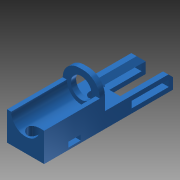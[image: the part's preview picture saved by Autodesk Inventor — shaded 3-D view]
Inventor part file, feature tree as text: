
AUTODESK INVENTOR PART (.ipt)
format: ipt  version: 2013 SP2 (Build 170200200, 200)  size: 194,560 bytes
history: native  units: in
note: dims shown in document units (in); Inventor stores cm internally (conversion verified against a paired STEP export)
features: extrude x10, sketch x8, fillet x1, chamfer x1
ambient origin geometry x8: Origin, YZ Plane, XZ Plane, XY Plane, X Axis, Y Axis, Z Axis, Center Point
bodies: Solid1 (feature_tree)
feature tree (20):
  sketch  "Sketch1"  dims[d5=1.063in d6=0.0in d11=0.5512in]
  extrude  "Extrusion1"  Depth=0.5512in
  extrude  "Extrusion6"  Depth=0.0787in
  extrude  "Extrusion5"  Depth=0.7087in
  extrude  "Extrusion7"  Depth=0.8661in
  fillet  "Fillet1"  Radius=0.0984in
  extrude  "Extrusion8"  Depth=0.315in
  extrude  "Extrusion9"  Depth=0.0984in
  extrude  "Extrusion10"  Depth=0.0787in TaperAngle=0.0deg
  extrude  "Extrusion11"  Depth=1.2992in TaperAngle=0.0deg
  extrude  "Extrusion12"  Depth=1.1811in TaperAngle=0.0deg
  extrude  "Extrusion13"  Depth=0.9055in
  chamfer  "Chamfer2"  [1 undecoded]
  sketch  "Sketch3"  dims[d12=0.3937in d13=0.0787in]
  sketch  "Sketch4"  dims[d18=0.5512in d19=0.7087in]
  sketch  "Sketch5"  dims[d20=1.1811in d21=0.0in d22=0.8661in d25=0.0984in d26=0.0in]
  sketch  "Sketch6"  dims[d27=0.0787in d28=0.0in d29=0.315in]
  sketch  "Sketch7"  dims[d32=0.2362in d33=0.0984in]
  sketch  "Sketch8"  dims[d34=0.0394in d35=0.0787in d36=0.0in]
  sketch  "Sketch9"  dims[d37=0.2953in d38=1.2992in d39=0.0in d41=1.1811in d42=0.0in d45=0.9055in d47=0.0in d49=0.126in d51=0.3937in d52=0.0in d55=0.7087in d56=0.2362in d57=0.2362in d58=0.1575in d59=1.3386in d60=0.3937in d61=0.0in d62=0.126in d63=0.126in d64=0.1575in d65=0.0in d69=0.3307in d70=0.7874in d71=0.0866in d72=0.0787in d73=45.0deg]
note: 1 required parameter value undecoded (feature->parameter linkage not recoverable at this tier; creation-order binding heuristic only, values carry confidence <= 0.55)
